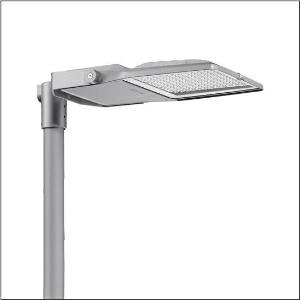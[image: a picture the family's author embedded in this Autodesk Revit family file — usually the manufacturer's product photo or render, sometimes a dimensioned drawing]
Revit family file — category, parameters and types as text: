
# Revit family: floodlight_fl_21_iq_midi___pl52_5xa7782f2d3a_028a
name_source: partatom
category: Lighting Fixtures
units: mm (PartAtom-declared; Revit-internal decimal feet)

## family parameters
Cut with Voids When Loaded = No
Host = Face
Light Source = No
Part Type = Normal
Room Calculation Point = No
Round Connector Dimension = Use Diameter
Shared = No

## types (1)
- --- (1 x LED, 35760 lm, 270.2 W, 3000K)
    Apparent Load = 270 VA
    CIE Flux Codes = 26 60 98 100 100
    Color Rendering = 70
    Color Temperature = 3000K
    Default Elevation = 1800 mm
    Description = Floodlight FL 21 iQ midi, floodlight, primary light control with lens, of PMMA, primary optical cover: protective disc, of toughened safety glass, transparent, light distribution: PL52, light emission: direct distribution, installation type: surface-mounted, LED, High Power LED, rated luminous flux: 35.760lm, luminous efficacy: 132lm/W, light colour: 730, colour temperature: 3000K, control gear: ECG iQ, control: optimised constant luminous flux control (CLO 2.0), Desk-Remote (wireless, voltage-free reading and setting of iQ features in the workshop via application-optimized NFC function/RFID function), Smart-Wire, Night-Set, Temp-Guard, Auto-Match, Street-Remote, with terminal, 6-pole, mains connection: 220..240V, AC, 50/60Hz, start of lifetime: 270W, end of service life: 287W, reduction: 117W, luminaire housing, of diecast aluminium, powder-coated, Siteco® metallic grey (DB 702S), corrosivity category C5 mid according to DIN EN ISO 12944, sealing non-destructively replaceable, please order mast flange separately, mast bracket, of steel, galvanised, powder-coated, Siteco® metallic grey (DB 702S), protection rating (complete): IP66, insulation class (complete): insulation class II (safety insulation), certification: CE, ENEC, VDE, protection symbol: D, impact resistance: IK08, permissible operating ambient temperature: -40..+40°C, permissible operating ambient temperature for outdoor applications: -40..+50°C, standard: DIN EN 12944, LABS conformity tested according to VDMA 24364:2018-05, packaging unit: 1 piece

Light Distribution: PL52
    Height = 76 mm
    Lamp = 1 x LED
    Lamp Light Flux = 35760 lm
    Lamp Power = 270.2 W
    Lamp count = 1
    Length = 657 mm
    Luminous efficacy = 132 lm/W
    Manufacturer = Siteco
    ModVariant = No
    Model = 5XA7782F2D3A
    Number of Poles = 1
    OnlyDefault = Yes
    Power Factor = 1
    Product Name = Floodlight FL 21 iQ midi | PL52
    Product group = floodlight | pylon annexe
    ProductGroupID = 6200
    Protection Class = Protection class II
    Protection Degree = IP 66
    RLX_Detail_Level = 1
    RLX_Emergency_Light_Flux = 0 lm
    RLX_Emergency_Type = 0
    RLX_Emergency_Type_DB = No
    RlxData = <blob elided: 153793 chars, md5=6800fd27>
    Socket = socket
    Standby Power = 0 W
    System Light Flux = 35760 lm
    System Power = 270 W
    Type Comments = factory setting: luminous flux: 100 % | dim-lin: 254 | 620 mA
    Type Image = l_1007123.jpg
    URL = http://relux.com
    VarID = @adj_074483
    Voltage = 0 V
    Weight = 0.00 kg
    Width = 442 mm

## geometry (parser evidence)
native form markers: Blend x4, Sweep x14
no freeform markers — native parametric forms only
